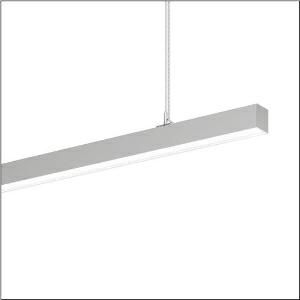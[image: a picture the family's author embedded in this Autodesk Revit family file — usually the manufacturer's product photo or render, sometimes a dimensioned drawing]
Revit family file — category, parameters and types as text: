
# Revit family: silica_r__21_51mx33tbt9s_9dae
name_source: partatom
category: Lighting Fixtures
units: mm (PartAtom-declared; Revit-internal decimal feet)

## family parameters
Cut with Voids When Loaded = No
Host = Face
Light Source = No
Part Type = Normal
Room Calculation Point = No
Round Connector Dimension = Use Diameter
Shared = No

## types (1)
- --- (1 x LED, 7170 lm, 67.4 W, 6500K)
    Apparent Load = 67 VA
    CIE Flux Codes = 78 96 99 56 100
    Color Rendering = 80
    Color Temperature = 6500K
    Default Elevation = 1800 mm
    Description = Silica® 21, office luminaire, primary optical cover: prismatic diffuser, of PMMA, CAT 2 (L<= 3000cd/m²), light emission: direct/indirect distribution, primary light characteristic: symmetric, installation type: suspended mounting, LED, rated luminous flux: 7.170lm, luminous efficacy: 101lm/W, light colour: 8tw, colour temperature: 2700..6500K, control gear: ECG DALI, with terminal, 3+2-pole, max. 2.5mm², mains connection: 220..240V, AC, 50/60Hz, rated input power: 70.8W, luminaire housing, of aluminium, metallic grey (RAL 9006), length: 1.504mm, width: 53mm, height: 53mm, protection rating (complete): IP20, insulation class (complete): insulation class I (protective earthing), certification: CE, permissible operating ambient temperature: 0..+35°C, standard: EN 50419, packaging unit: 1 piece
    Height = 53 mm
    Lamp = 1 x LED
    Lamp Light Flux = 7170 lm
    Lamp Power = 67.4 W
    Lamp count = 1
    Length = 1504 mm
    Luminous efficacy = 106 lm/W
    Manufacturer = Siteco
    ModVariant = No
    Model = 51MX33TBT9S
    Mounting Place = Ceiling
    Mounting Type = Pendant
    Number of Poles = 1
    OnlyDefault = Yes
    Power Factor = 1
    Product Name = Silica® 21
    Product group = office luminaire | ceiling pendant
    ProductGroupID = 902
    Protection Class = Protection class I
    Protection Degree = IP 20
    RLX_Detail_Level = 1
    RLX_Emergency_Light_Flux = 0 lm
    RLX_Emergency_Type = 0
    RLX_Emergency_Type_DB = No
    RlxData = <blob elided: 20181 chars, md5=22d6741e>
    Socket = socket
    Standby Power = 0 W
    System Light Flux = 7170 lm
    System Power = 67 W
    Type Comments = individual setting
    Type Image = l_1335864.jpg
    URL = http://relux.com
    VarID = @adj_109543
    Voltage = 0 V
    Weight = 0.00 kg
    Width = 53 mm

## geometry (parser evidence)
native form markers: Blend x4, Sweep x13
no freeform markers — native parametric forms only
